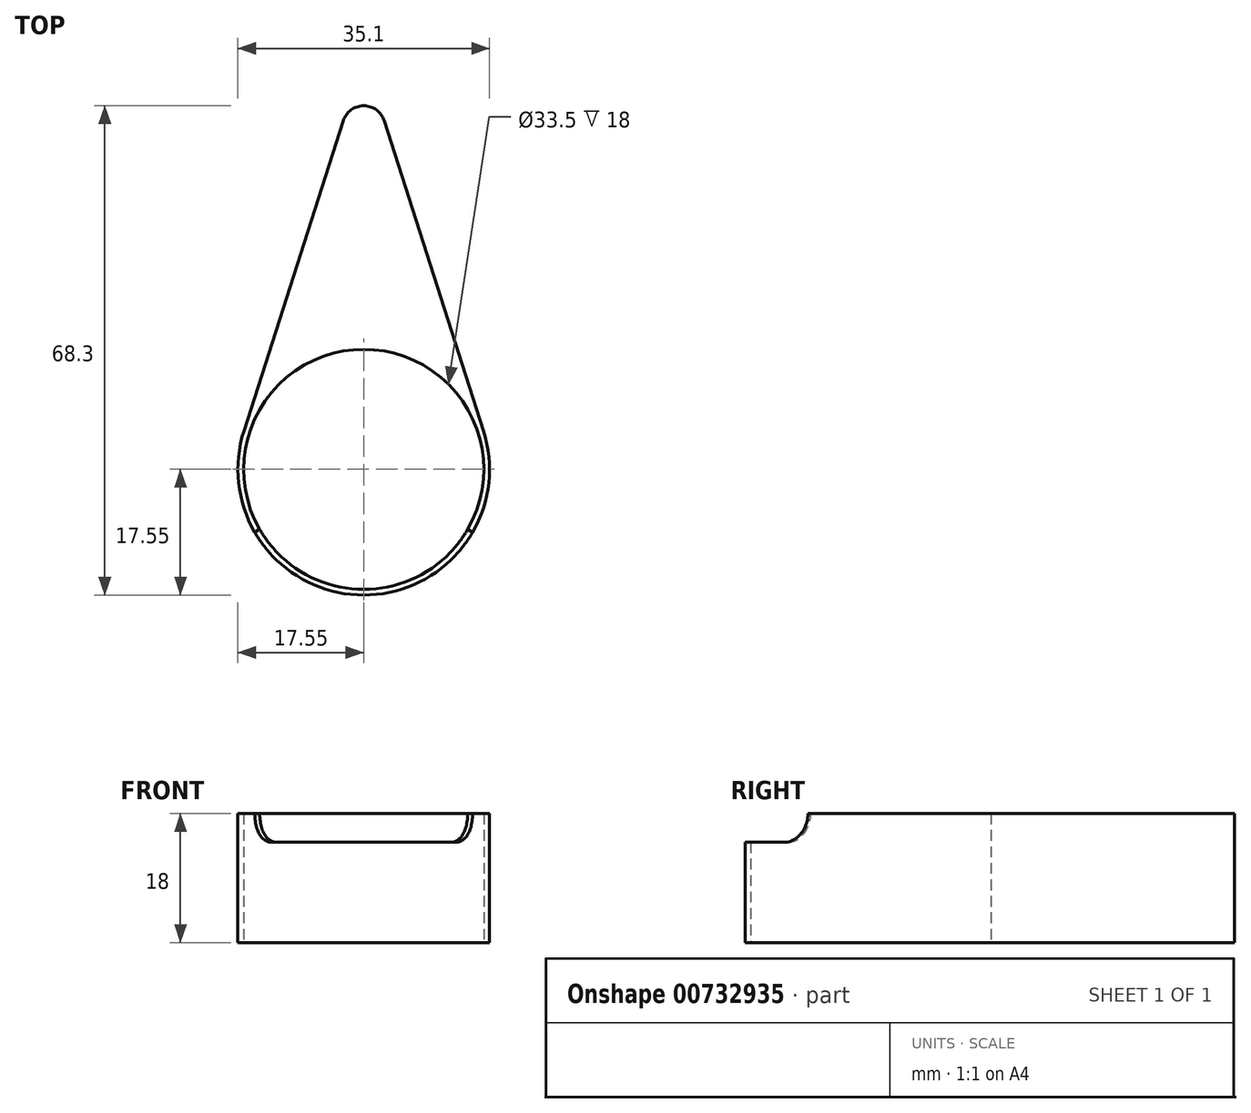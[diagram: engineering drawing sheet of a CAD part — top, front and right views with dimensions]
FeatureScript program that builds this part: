
annotation { "Feature Type Name" : "Feature", "Feature Type Description" : "" }
export const myFeature = defineFeature(function(context is Context, id is Id, definition is map)
    precondition{}
    {
        {
            var Q0;
            Q0=qCreatedBy(makeId("Top.planeOp"),FACE);
            var sketch = newSketch(context, id + "F0", { "sketchPlane" : qUnion([Q0])});
            skCircle(sketch, "E0", {"center": v(0, 0) * mm, "radius": 16.75 * mm});
            skArc(sketch, "E1", {"start": v(-16.72, 5.35) * mm, "mid": v(0, -17.55) * mm, "end": v(16.72, 5.35) * mm});
            skLineSegment(sketch, "E2", {"start": v(-16.72, 5.35) * mm, "end": v(-2.86, 48.66) * mm});
            skLineSegment(sketch, "E3", {"start": v(2.86, 48.66) * mm, "end": v(16.72, 5.35) * mm});
            skArc(sketch, "E4", {"start": v(2.86, 48.66) * mm, "mid": v(0, 50.75) * mm, "end": v(-2.86, 48.66) * mm});
            skLineSegment(sketch, "E5", {"start": v(0, 0) * mm, "end": v(0, 47.75) * mm, "construction": true});
            skLineSegment(sketch, "E6", {"start": v(0, 50.75) * mm, "end": v(0, 47.75) * mm, "construction": true});
            skPoint(sketch, "E7", {"position": v(0, 16.75) * mm});
            skSolve(sketch);
        }
        {
            var Q0;
            Q0 = qSketchRegion(id + "F0", true);
            extrude(context, id + "F1", {"entities" : qUnion([Q0]), "depth" : 17 * mm, "offsetDistance" : 25 * mm, "hasSecondDirection" : true, "secondDirectionOppositeDirection" : true, "secondDirectionDepth" : 18 * mm});
        }
        {
            var Q0;
            Q0=qCreatedBy(makeId("Top.planeOp"),FACE);
            var sketch = newSketch(context, id + "F2", { "sketchPlane" : qUnion([Q0])});
            skLineSegment(sketch, "E8", {"start": v(0, 0) * mm, "end": v(15.2, -8.78) * mm});
            skLineSegment(sketch, "E9", {"start": v(-15.2, -8.78) * mm, "end": v(0, 0) * mm});
            skArc(sketch, "E10", {"start": v(-15.2, -8.78) * mm, "mid": v(0, -17.55) * mm, "end": v(15.2, -8.78) * mm});
            skLineSegment(sketch, "E11", {"start": v(0, 0) * mm, "end": v(0, -17.55) * mm, "construction": true});
            skSolve(sketch);
        }
        {
            var Q0;
            Q0 = qSketchRegion(id + "F2", true);
            extrude(context, id + "F3", {"entities" : qUnion([Q0]), "operationType" : NewBodyOperationType.REMOVE, "depth" : 4 * mm, "offsetDistance" : 25 * mm, "hasSecondDirection" : true, "secondDirectionOppositeDirection" : true, "secondDirectionDepth" : 4 * mm});
        }
        {
            var Q0;
            Q0=makeQuery(id+"F3.boolean.opBoolean","COPY",EDGE,{"derivedFrom":makeQuery(id+"F3.opExtrude","CAP_EDGE",EDGE,{"disambiguationData":[OSD([sQuery(id+"F2.wireOp",EDGE,"E9")])],"isStart":false})});
            var Q1;
            Q1=makeQuery(id+"F3.boolean.opBoolean","COPY",EDGE,{"derivedFrom":makeQuery(id+"F3.opExtrude","CAP_EDGE",EDGE,{"disambiguationData":[OSD([sQuery(id+"F2.wireOp",EDGE,"E9")])],"isStart":true})});
            var Q2;
            Q2=makeQuery(id+"F3.boolean.opBoolean","COPY",EDGE,{"derivedFrom":makeQuery(id+"F3.opExtrude","CAP_EDGE",EDGE,{"disambiguationData":[OSD([sQuery(id+"F2.wireOp",EDGE,"E8")])],"isStart":true})});
            var Q3;
            Q3=makeQuery(id+"F3.boolean.opBoolean","COPY",EDGE,{"derivedFrom":makeQuery(id+"F3.opExtrude","CAP_EDGE",EDGE,{"disambiguationData":[OSD([sQuery(id+"F2.wireOp",EDGE,"E8")])],"isStart":false})});
            fillet(context, id + "F4", {"entities" : qUnion([Q0, Q1, Q2, Q3]), "radius" : 4 * mm, "tangentPropagation" : true, "allowEdgeOverflow" : false});
        }
        {
            var Q0;
            Q0=qCreatedBy(makeId("Top.planeOp"),FACE);
            var sketch = newSketch(context, id + "F5", { "sketchPlane" : qUnion([Q0])});
            skCircle(sketch, "E12", {"center": v(0, 0) * mm, "radius": 55.05 * mm});
            skSolve(sketch);
        }
        {
            var Q0;
            Q0=makeQuery(id+"F1.opExtrude","SWEPT_FACE",FACE,{"disambiguationData":[OSD([sQuery(id+"F0.wireOp",EDGE,"E3")])]});
            var sketch = newSketch(context, id + "F6", { "sketchPlane" : qUnion([Q0])});
            skSolve(sketch);
        }
        {
            var Q0;
            Q0 = qSketchRegion(id + "F6", true);
            var Q1;
            Q1=makeQuery(id+"F5.imprint","IMPRINT",FACE,{"disambiguationData":[TD([[makeQuery(id+"F5.imprint","IMPRINT",EDGE,{"derivedFrom":sQuery(id+"F5.wireOp",EDGE,"E12")}),1.0]])]});
            extrude(context, id + "F7", {"entities" : qUnion([Q0, Q1]), "operationType" : NewBodyOperationType.REMOVE, "depth" : 25 * mm, "offsetDistance" : 25 * mm});
        }
    });
